# Revit family: NLRS_33_GM_FB_TC_STORAX_vloerluik_CLA_BCB
name_source: partatom
category: Generic Models
revit_build: Autodesk Revit 2014 (Build: 20130308_1515(x64)
units: mm (PartAtom-declared; Revit-internal decimal feet)

## types (9) — shared parameters
Manufacturer = Storax
Model = BV
URL = http://www.storax.nl
belasting = 15 kN
binnenluik = tbv traanplaat
brandwerend 90 min = nee
gasdrukveer = nee
geïsoleerd = nee
materiaal = bcb_aluminium
productgroep = Vloerluiken
rubberen_afdichting = enkel
scharnierend = nee
vergrendeling = nee
vullen_met_beton = ja
zero-valued in all types: Default Elevation

## per-type parameters (varying)
| type | binnenmaat_breedte | binnenmaat_lengte | gewicht | sluiting | sluiting hoek | sluiting x-as | sluiting y-as | uitwendige_breedte | uitwendige_lengte |
| CLA 33 | 300 mm | 300 mm | 5 | 2 | No | Yes | No | 420 mm  [stored 1.37795 ft] | 420 mm  [stored 1.37795 ft] |
| CLA 44 | 400 mm  [stored 1.31234 ft] | 400 mm  [stored 1.31234 ft] | 7 | 4 | Yes | No | No | 520 mm | 520 mm |
| CLA 64 | 600 mm | 400 mm  [stored 1.31234 ft] | 9 | 4 | Yes | No | No | 720 mm | 520 mm |
| CLA 55 | 500 mm  [stored 1.64042 ft] | 500 mm  [stored 1.64042 ft] | 9 | 4 | Yes | No | No | 620 mm | 620 mm |
| CLA 66 | 600 mm | 600 mm | 10 | 4 | Yes | No | No | 720 mm | 720 mm |
| CLA 86 | 800 mm | 600 mm | 12 | 6 | Yes | No | Yes | 920 mm | 720 mm |
| CLA 88 | 800 mm | 800 mm | 15 | 8 | Yes | Yes | Yes | 920 mm | 920 mm |
| CLA 106 | 1000 mm  [stored 3.28084 ft] | 600 mm | 12 | 6 | Yes | No | Yes | 1120 mm | 720 mm |
| maatwerk | 1000 mm  [stored 3.28084 ft] | 600 mm | 0 | 0 | Yes | Yes | Yes | 1120 mm | 720 mm |

note: [stored X ft] marks values corroborated as IEEE doubles in the binary element streams (Revit-internal decimal feet)

## geometry (parser evidence)
native form markers: Blend x809, Sweep x4
no freeform markers — native parametric forms only
